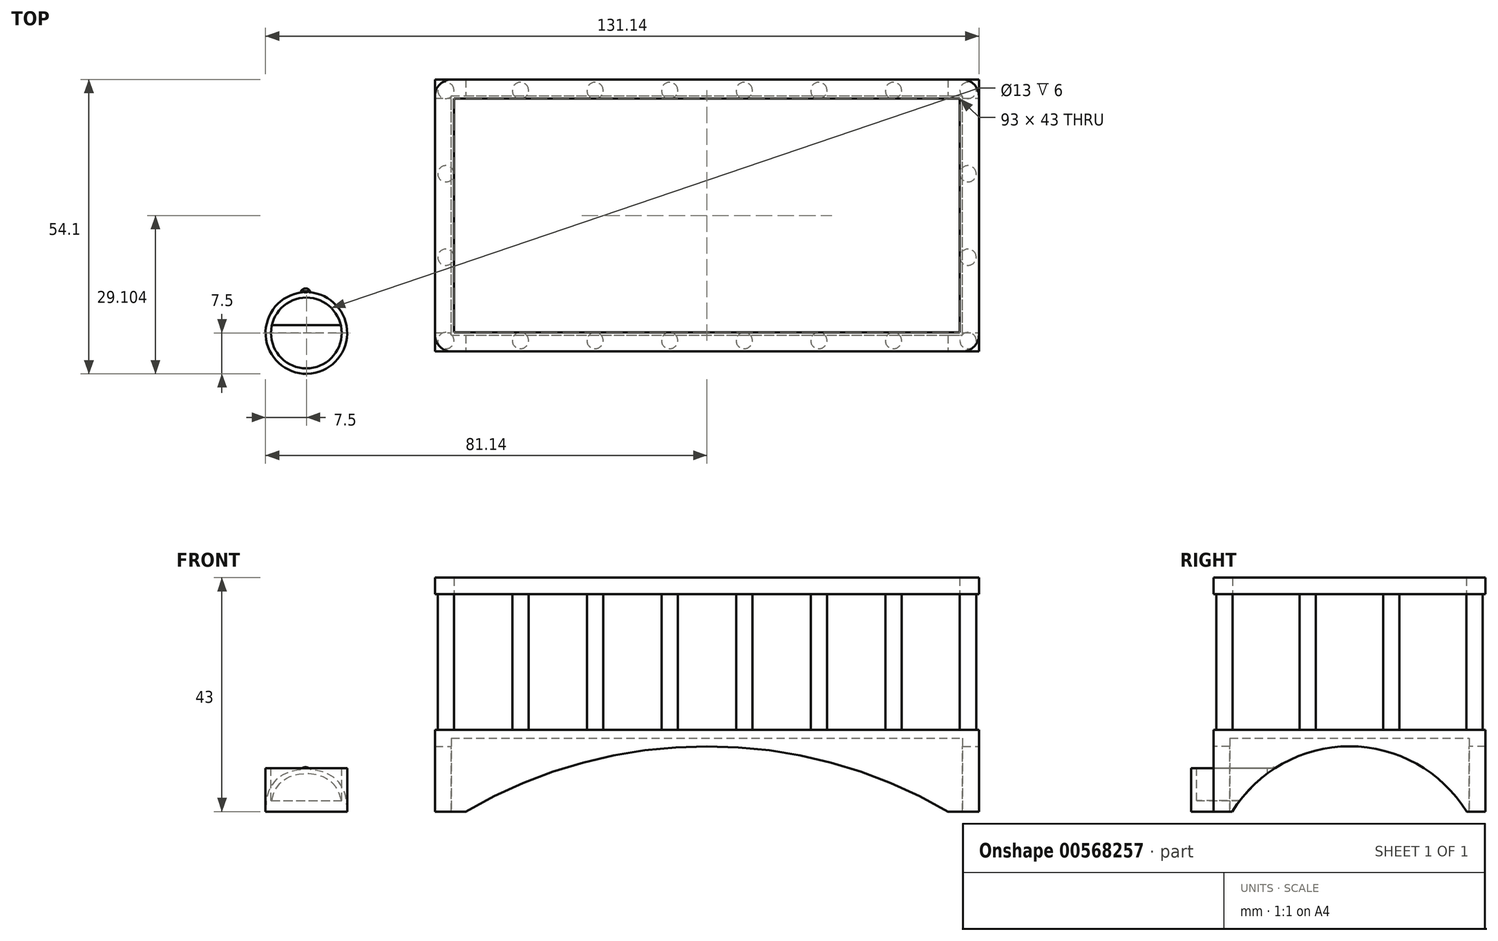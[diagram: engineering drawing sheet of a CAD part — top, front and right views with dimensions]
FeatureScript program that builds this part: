
annotation { "Feature Type Name" : "Feature", "Feature Type Description" : "" }
export const myFeature = defineFeature(function(context is Context, id is Id, definition is map)
    precondition{}
    {
        {
            var Q0;
            Q0=qCreatedBy(makeId("Top.planeOp"),FACE);
            var sketch = newSketch(context, id + "F0", { "sketchPlane" : qUnion([Q0])});
            skCircle(sketch, "E0", {"center": v(-44.1, -10.35) * mm, "radius": 7.5 * mm});
            skSolve(sketch);
        }
        {
            var Q0;
            Q0 = qSketchRegion(id + "F0", true);
            extrude(context, id + "F1", {"entities" : qUnion([Q0]), "depth" : 8 * mm, "offsetDistance" : 25 * mm});
        }
        {
            var Q0;
            Q0=makeQuery(id+"F1.opExtrude","CAP_FACE",FACE,{"disambiguationData":[OSD([sQuery(id+"F0.wireOp",EDGE,"E0")])],"isStart":false});
            var sketch = newSketch(context, id + "F2", { "sketchPlane" : qUnion([Q0])});
            skCircle(sketch, "E1", {"center": v(-44.1, -10.35) * mm, "radius": 6.5 * mm});
            skSolve(sketch);
        }
        {
            var Q0;
            Q0 = qSketchRegion(id + "F2", true);
            extrude(context, id + "F3", {"entities" : qUnion([Q0]), "operationType" : NewBodyOperationType.REMOVE, "oppositeDirection" : true, "depth" : 6 * mm, "offsetDistance" : 25 * mm});
        }
        {
            var Q0;
            Q0=qCreatedBy(makeId("Front.planeOp"),FACE);
            var sketch = newSketch(context, id + "F4", { "sketchPlane" : qUnion([Q0])});
            skCircle(sketch, "E2", {"center": v(-44.26, 6.91) * mm, "radius": 1.25 * mm});
            skSolve(sketch);
        }
        {
            var Q0;
            Q0 = qSketchRegion(id + "F4", true);
            var Q1;
            Q1=makeQuery(id+"F1.opExtrude","SWEPT_FACE",FACE,{"disambiguationData":[OSD([sQuery(id+"F0.wireOp",EDGE,"E0")])]});
            extrude(context, id + "F5", {"entities" : qUnion([Q0]), "operationType" : NewBodyOperationType.ADD, "endBound" : BoundingType.UP_TO_SURFACE, "depth" : 25 * mm, "endBoundEntityFace" : qUnion([Q1]), "offsetDistance" : 25 * mm, "hasSecondDirection" : true, "secondDirectionOppositeDirection" : true, "secondDirectionDepth" : 10 * mm});
        }
        {
            var Q0;
            {var subQ0=sQuery(id+"F4.wireOp",EDGE,"E2");Q0=makeQuery(id+"F5.boolean.opBoolean","SPLIT",EDGE,{"disambiguationData":[topologyDisambiguationEdgeConnected([makeQuery(id+"F5.opExtrude","CAP_FACE",FACE,{"disambiguationData":[OSD([subQ0])],"isStart":false})])],"derivedFrom":makeQuery(id+"F5.opExtrude","CAP_EDGE",EDGE,{"disambiguationData":[OSD([subQ0])],"isStart":false})});}
            chamfer(context, id + "F6", {"entities" : qUnion([Q0]), "width" : 0.15 * mm, "tangentPropagation" : true});
        }
        {
            var Q0;
            Q0=qCreatedBy(makeId("Top.planeOp"),FACE);
            var sketch = newSketch(context, id + "F7", { "sketchPlane" : qUnion([Q0])});
            skLineSegment(sketch, "E3.bottom", {"start": v(-20.46, -13.75) * mm, "end": v(79.54, -13.75) * mm});
            skLineSegment(sketch, "E3.top", {"start": v(-20.46, 36.25) * mm, "end": v(79.54, 36.25) * mm});
            skLineSegment(sketch, "E3.left", {"start": v(-20.46, -13.75) * mm, "end": v(-20.46, 36.25) * mm});
            skLineSegment(sketch, "E3.right", {"start": v(79.54, -13.75) * mm, "end": v(79.54, 36.25) * mm});
            skSolve(sketch);
        }
        {
            var Q0;
            Q0 = qSketchRegion(id + "F7", true);
            extrude(context, id + "F8", {"entities" : qUnion([Q0]), "depth" : 15 * mm, "offsetDistance" : 25 * mm});
        }
        {
            var Q0;
            Q0=makeQuery(id+"F8.opExtrude","CAP_FACE",FACE,{"disambiguationData":[OSD([sQuery(id+"F7.wireOp",EDGE,"E3.bottom"),sQuery(id+"F7.wireOp",EDGE,"E3.top"),sQuery(id+"F7.wireOp",EDGE,"E3.left"),sQuery(id+"F7.wireOp",EDGE,"E3.right")])],"isStart":true});
            var sketch = newSketch(context, id + "F9", { "sketchPlane" : qUnion([Q0])});
            skLineSegment(sketch, "E4.bottom", {"start": v(-17.46, 10.75) * mm, "end": v(76.54, 10.75) * mm});
            skLineSegment(sketch, "E4.top", {"start": v(-17.46, -33.25) * mm, "end": v(76.54, -33.25) * mm});
            skLineSegment(sketch, "E4.left", {"start": v(-17.46, 10.75) * mm, "end": v(-17.46, -33.25) * mm});
            skLineSegment(sketch, "E4.right", {"start": v(76.54, 10.75) * mm, "end": v(76.54, -33.25) * mm});
            skSolve(sketch);
        }
        {
            var Q0;
            Q0 = qSketchRegion(id + "F9", true);
            extrude(context, id + "F10", {"entities" : qUnion([Q0]), "operationType" : NewBodyOperationType.REMOVE, "oppositeDirection" : true, "depth" : 13.5 * mm, "offsetDistance" : 25 * mm});
        }
        {
            var Q0;
            Q0=makeQuery(id+"F8.opExtrude","SWEPT_FACE",FACE,{"disambiguationData":[OSD([sQuery(id+"F7.wireOp",EDGE,"E3.bottom")])]});
            var sketch = newSketch(context, id + "F11", { "sketchPlane" : qUnion([Q0])});
            skLineSegment(sketch, "E5", {"start": v(29.54, 15) * mm, "end": v(29.54, -75.83) * mm, "construction": true});
            skPoint(sketch, "E5.endSnap0", {"position": v(29.54, 0) * mm});
            skCircle(sketch, "E6", {"center": v(29.54, -75.83) * mm, "radius": 87.83 * mm});
            skSolve(sketch);
        }
        {
            var Q0;
            Q0 = qSketchRegion(id + "F11", true);
            extrude(context, id + "F12", {"entities" : qUnion([Q0]), "operationType" : NewBodyOperationType.REMOVE, "endBound" : BoundingType.THROUGH_ALL, "oppositeDirection" : true, "depth" : 25 * mm, "offsetDistance" : 25 * mm});
        }
        {
            var Q0;
            Q0=makeQuery(id+"F8.opExtrude","SWEPT_FACE",FACE,{"disambiguationData":[OSD([sQuery(id+"F7.wireOp",EDGE,"E3.right")])]});
            var sketch = newSketch(context, id + "F13", { "sketchPlane" : qUnion([Q0])});
            skLineSegment(sketch, "E7", {"start": v(11.25, 15) * mm, "end": v(11.25, -126.55) * mm, "construction": true});
            skCircle(sketch, "E8", {"center": v(11.25, -13.33) * mm, "radius": 25.33 * mm});
            skSolve(sketch);
        }
        {
            var Q0;
            Q0 = qSketchRegion(id + "F13", true);
            extrude(context, id + "F14", {"entities" : qUnion([Q0]), "operationType" : NewBodyOperationType.REMOVE, "endBound" : BoundingType.THROUGH_ALL, "oppositeDirection" : true, "depth" : 25 * mm, "offsetDistance" : 25 * mm});
        }
        {
            var Q0;
            Q0=makeQuery(id+"F8.opExtrude","CAP_FACE",FACE,{"disambiguationData":[OSD([sQuery(id+"F7.wireOp",EDGE,"E3.bottom"),sQuery(id+"F7.wireOp",EDGE,"E3.top"),sQuery(id+"F7.wireOp",EDGE,"E3.left"),sQuery(id+"F7.wireOp",EDGE,"E3.right")])],"isStart":false});
            var sketch = newSketch(context, id + "F15", { "sketchPlane" : qUnion([Q0])});
            skCircle(sketch, "E9", {"center": v(-18.46, -11.75) * mm, "radius": 1.5 * mm});
            skCircle(sketch, "E10.2.0.0", {"center": v(-4.75, -11.75) * mm, "radius": 1.5 * mm});
            skCircle(sketch, "E10.4.0.0", {"center": v(8.97, -11.75) * mm, "radius": 1.5 * mm});
            skCircle(sketch, "E10.6.0.0", {"center": v(22.68, -11.75) * mm, "radius": 1.5 * mm});
            skCircle(sketch, "E10.8.0.0", {"center": v(36.4, -11.75) * mm, "radius": 1.5 * mm});
            skCircle(sketch, "E10.10.0.0", {"center": v(50.11, -11.75) * mm, "radius": 1.5 * mm});
            skCircle(sketch, "E10.12.0.0", {"center": v(63.83, -11.75) * mm, "radius": 1.5 * mm});
            skCircle(sketch, "E10.14.0.0", {"center": v(77.54, -11.75) * mm, "radius": 1.5 * mm});
            skLineSegment(sketch, "E11", {"start": v(79.54, 11.25) * mm, "end": v(-1.55, 11.25) * mm, "construction": true});
            skLineSegment(sketch, "E12", {"start": v(29.54, 36.25) * mm, "end": v(29.54, -3.9) * mm, "construction": true});
            skCircle(sketch, "E13.0.2.0", {"center": v(-18.46, 3.59) * mm, "radius": 1.5 * mm});
            skCircle(sketch, "E13.0.4.0", {"center": v(-18.46, 18.92) * mm, "radius": 1.5 * mm});
            skCircle(sketch, "E14.MirrorC", {"center": v(77.54, 3.59) * mm, "radius": 1.5 * mm});
            skCircle(sketch, "E15.MirrorC", {"center": v(77.54, 18.92) * mm, "radius": 1.5 * mm});
            skLineSegment(sketch, "E16.MirrorCS", {"start": v(-18.46, 34.25) * mm, "end": v(6.54, 34.25) * mm, "construction": true});
            skLineSegment(sketch, "E17.MirrorCS", {"start": v(-18.46, 34.25) * mm, "end": v(-11.6, 34.25) * mm, "construction": true});
            skCircle(sketch, "E18.MirrorC", {"center": v(50.11, 34.25) * mm, "radius": 1.5 * mm});
            skCircle(sketch, "E19.MirrorC", {"center": v(36.4, 34.25) * mm, "radius": 1.5 * mm});
            skCircle(sketch, "E20.MirrorC", {"center": v(63.83, 34.25) * mm, "radius": 1.5 * mm});
            skCircle(sketch, "E21.MirrorC", {"center": v(22.68, 34.25) * mm, "radius": 1.5 * mm});
            skCircle(sketch, "E22.MirrorC", {"center": v(8.97, 34.25) * mm, "radius": 1.5 * mm});
            skCircle(sketch, "E23.MirrorC", {"center": v(-4.75, 34.25) * mm, "radius": 1.5 * mm});
            skCircle(sketch, "E24.MirrorC", {"center": v(-18.46, 34.25) * mm, "radius": 1.5 * mm});
            skCircle(sketch, "E25.MirrorC", {"center": v(77.54, 34.25) * mm, "radius": 1.5 * mm});
            skSolve(sketch);
        }
        {
            var Q0;
            Q0 = qSketchRegion(id + "F15", true);
            extrude(context, id + "F16", {"entities" : qUnion([Q0]), "operationType" : NewBodyOperationType.ADD, "depth" : 25 * mm, "offsetDistance" : 25 * mm});
        }
        {
            var Q0;
            Q0=makeQuery(id+"F16.opExtrude","CAP_FACE",FACE,{"disambiguationData":[OSD([sQuery(id+"F15.wireOp",EDGE,"E9")])],"isStart":false});
            var sketch = newSketch(context, id + "F17", { "sketchPlane" : qUnion([Q0])});
            skLineSegment(sketch, "E26.bottom", {"start": v(-20.46, -13.75) * mm, "end": v(79.54, -13.75) * mm});
            skLineSegment(sketch, "E26.top", {"start": v(-20.46, 36.25) * mm, "end": v(79.54, 36.25) * mm});
            skLineSegment(sketch, "E26.left", {"start": v(-20.46, -13.75) * mm, "end": v(-20.46, 36.25) * mm});
            skLineSegment(sketch, "E26.right", {"start": v(79.54, -13.75) * mm, "end": v(79.54, 36.25) * mm});
            skLineSegment(sketch, "E27.bottom", {"start": v(-16.96, 32.75) * mm, "end": v(76.04, 32.75) * mm});
            skLineSegment(sketch, "E27.top", {"start": v(-16.96, -10.25) * mm, "end": v(76.04, -10.25) * mm});
            skLineSegment(sketch, "E27.left", {"start": v(-16.96, 32.75) * mm, "end": v(-16.96, -10.25) * mm});
            skLineSegment(sketch, "E27.right", {"start": v(76.04, 32.75) * mm, "end": v(76.04, -10.25) * mm});
            skSolve(sketch);
        }
        {
            var Q0;
            Q0 = qSketchRegion(id + "F17", true);
            extrude(context, id + "F18", {"entities" : qUnion([Q0]), "operationType" : NewBodyOperationType.ADD, "depth" : 3 * mm, "offsetDistance" : 25 * mm});
        }
        {
            var Q0;
            Q0=makeQuery(id+"F18.opExtrude","SWEPT_EDGE",EDGE,{"disambiguationData":[OSD([sQuery(id+"F17.wireOp",EDGE,"E26.bottom"),sQuery(id+"F17.wireOp",EDGE,"E26.left")])]});
            fillet(context, id + "F19", {"entities" : qUnion([Q0]), "radius" : 3 * mm, "tangentPropagation" : true, "allowEdgeOverflow" : false});
        }
        {
            var Q0;
            Q0=makeQuery(id+"F18.opExtrude","SWEPT_EDGE",EDGE,{"disambiguationData":[OSD([sQuery(id+"F17.wireOp",EDGE,"E26.bottom"),sQuery(id+"F17.wireOp",EDGE,"E26.right")])]});
            var Q1;
            Q1=makeQuery(id+"F18.opExtrude","SWEPT_EDGE",EDGE,{"disambiguationData":[OSD([sQuery(id+"F17.wireOp",EDGE,"E26.top"),sQuery(id+"F17.wireOp",EDGE,"E26.right")])]});
            var Q2;
            Q2=makeQuery(id+"F18.opExtrude","SWEPT_EDGE",EDGE,{"disambiguationData":[OSD([sQuery(id+"F17.wireOp",EDGE,"E26.top"),sQuery(id+"F17.wireOp",EDGE,"E26.left")])]});
            fillet(context, id + "F20", {"entities" : qUnion([Q0, Q1, Q2]), "radius" : 3 * mm, "tangentPropagation" : true, "allowEdgeOverflow" : false});
        }
    });
